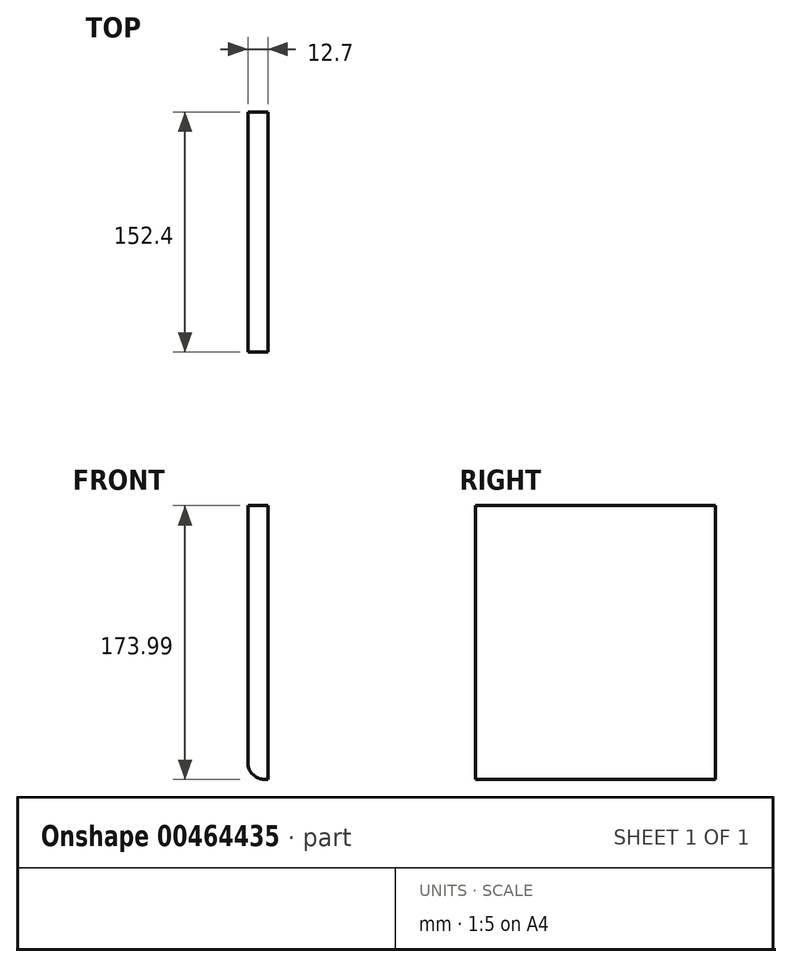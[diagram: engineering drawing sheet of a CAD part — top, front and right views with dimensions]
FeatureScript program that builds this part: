
annotation { "Feature Type Name" : "Feature", "Feature Type Description" : "" }
export const myFeature = defineFeature(function(context is Context, id is Id, definition is map)
    precondition{}
    {
        {
            var Q0;
            Q0=qCreatedBy(makeId("Front.planeOp"),FACE);
            var sketch = newSketch(context, id + "F0", { "sketchPlane" : qUnion([Q0])});
            skLineSegment(sketch, "E0", {"start": v(0, 0) * mm, "end": v(0, -163.32) * mm});
            skLineSegment(sketch, "E1", {"start": v(10.67, -174) * mm, "end": v(12.7, -174) * mm});
            skLineSegment(sketch, "E2", {"start": v(12.7, -174) * mm, "end": v(12.7, 0) * mm});
            skLineSegment(sketch, "E3", {"start": v(12.7, 0) * mm, "end": v(0, 0) * mm});
            skPoint(sketch, "E4.visualSharp", {"position": v(0, -174) * mm});
            skArc(sketch, "E4.filletArc", {"start": v(0, -163.32) * mm, "mid": v(3.12, -170.87) * mm, "end": v(10.67, -174) * mm});
            skSolve(sketch);
        }
        {
            var Q0;
            Q0=makeQuery(id+"F0.imprint","IMPRINT",FACE,{"disambiguationData":[TD([[makeQuery(id+"F0.imprint","IMPRINT",EDGE,{"derivedFrom":sQuery(id+"F0.wireOp",EDGE,"E0")}),1.0]])]});
            extrude(context, id + "F1", {"entities" : qUnion([Q0]), "depth" : 152.4 * mm});
        }
    });
